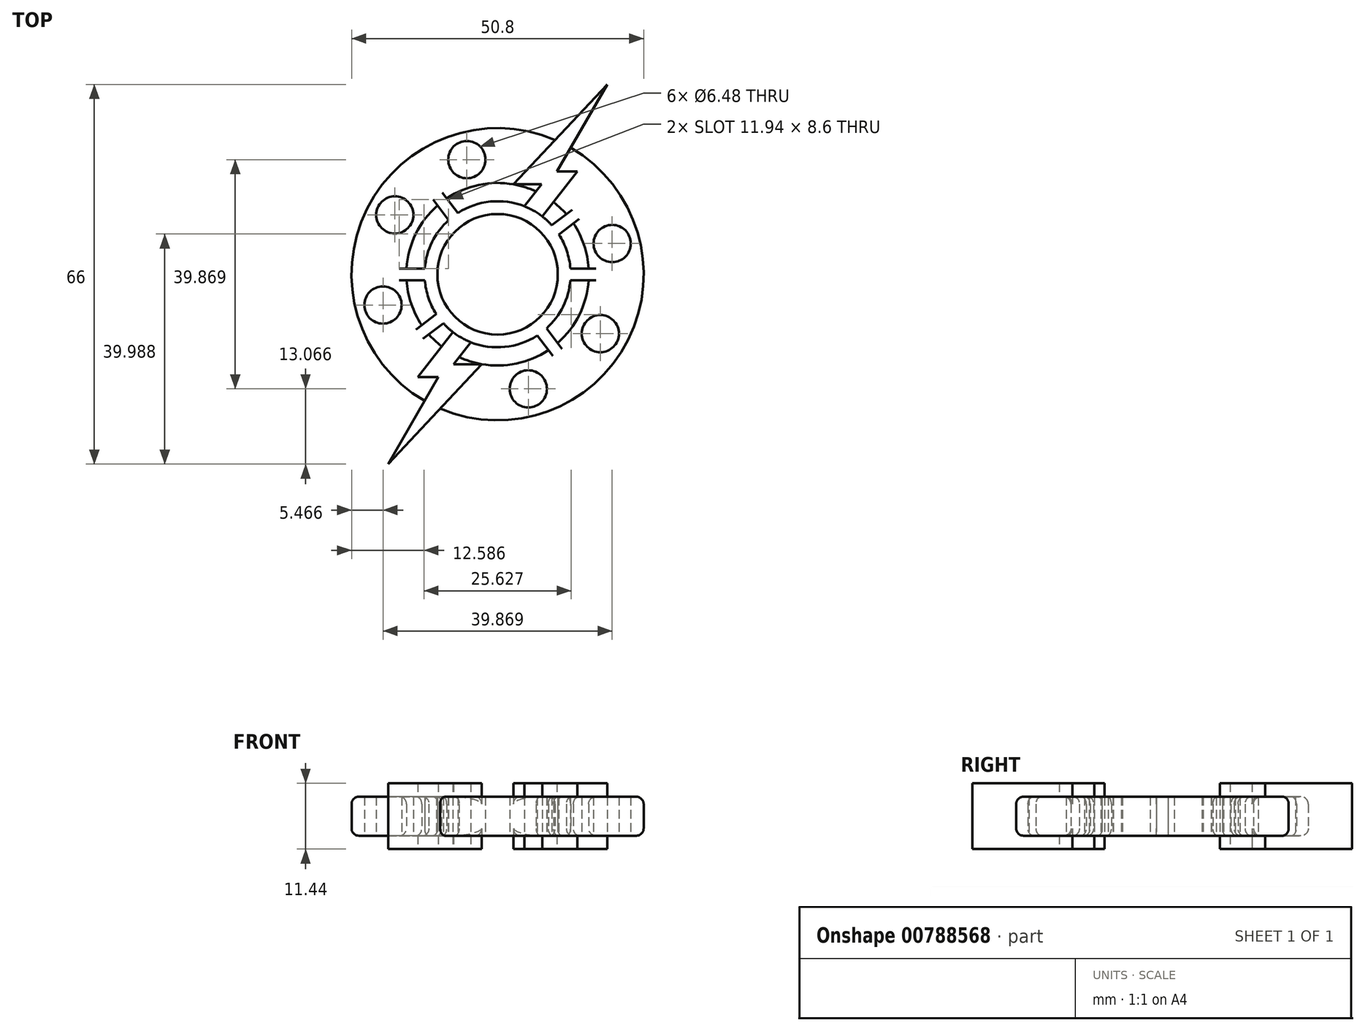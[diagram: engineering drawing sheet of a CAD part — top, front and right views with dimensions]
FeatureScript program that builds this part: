
annotation { "Feature Type Name" : "Feature", "Feature Type Description" : "" }
export const myFeature = defineFeature(function(context is Context, id is Id, definition is map)
    precondition{}
    {
        {
            var Q0;
            Q0=qCreatedBy(makeId("Top.planeOp"),FACE);
            var sketch = newSketch(context, id + "F0", { "sketchPlane" : qUnion([Q0])});
            skCircle(sketch, "E0", {"center": v(0, 0) * mm, "radius": 25.4 * mm});
            skCircle(sketch, "E1", {"center": v(0, 0) * mm, "radius": 15.88 * mm});
            skLineSegment(sketch, "E2", {"start": v(19.05, 33) * mm, "end": v(2.78, 15.63) * mm});
            skLineSegment(sketch, "E3", {"start": v(2.78, 15.63) * mm, "end": v(7.63, 15.63) * mm});
            skLineSegment(sketch, "E4", {"start": v(7.63, 15.63) * mm, "end": v(3.22, 9.97) * mm});
            skLineSegment(sketch, "E5", {"start": v(19.05, 33) * mm, "end": v(10.33, 17.89) * mm});
            skLineSegment(sketch, "E6", {"start": v(10.33, 17.89) * mm, "end": v(13.9, 17.89) * mm});
            skLineSegment(sketch, "E7", {"start": v(13.9, 17.89) * mm, "end": v(6.42, 8.28) * mm});
            skLineSegment(sketch, "E8.trimOffspring", {"start": v(10.33, 17.89) * mm, "end": v(19.05, 33) * mm});
            skLineSegment(sketch, "E9.1.0", {"start": v(-7.63, -15.63) * mm, "end": v(-3.22, -9.97) * mm});
            skLineSegment(sketch, "E9.1.1", {"start": v(-2.78, -15.63) * mm, "end": v(-7.63, -15.63) * mm});
            skLineSegment(sketch, "E9.1.2", {"start": v(-19.05, -33) * mm, "end": v(-2.78, -15.63) * mm});
            skLineSegment(sketch, "E9.1.3", {"start": v(-10.33, -17.89) * mm, "end": v(-19.05, -33) * mm});
            skLineSegment(sketch, "E9.1.4", {"start": v(-10.33, -17.89) * mm, "end": v(-13.9, -17.89) * mm});
            skLineSegment(sketch, "E9.1.5", {"start": v(-13.9, -17.89) * mm, "end": v(-6.42, -8.28) * mm});
            skCircle(sketch, "E10", {"center": v(0, 0) * mm, "radius": 10.48 * mm});
            skCircle(sketch, "E11", {"center": v(0, 0) * mm, "radius": 12.7 * mm});
            skLineSegment(sketch, "E12", {"start": v(0, 0) * mm, "end": v(19.05, 33) * mm, "construction": true});
            skLineSegment(sketch, "E13", {"start": v(0, 0) * mm, "end": v(-19.05, -33) * mm, "construction": true});
            skCircle(sketch, "E14", {"center": v(-17.87, 10.32) * mm, "radius": 3.24 * mm});
            skCircle(sketch, "E15", {"center": v(0, 0) * mm, "radius": 20.64 * mm, "construction": true});
            skCircle(sketch, "E16", {"center": v(-5.34, 19.93) * mm, "radius": 3.24 * mm});
            skCircle(sketch, "E17", {"center": v(-19.93, -5.34) * mm, "radius": 3.24 * mm});
            skCircle(sketch, "E18", {"center": v(5.34, -19.93) * mm, "radius": 3.24 * mm});
            skCircle(sketch, "E19", {"center": v(17.87, -10.32) * mm, "radius": 3.24 * mm});
            skCircle(sketch, "E20", {"center": v(19.93, 5.34) * mm, "radius": 3.24 * mm});
            skPoint(sketch, "E21.middle", {"position": v(-15.88, 0) * mm});
            skLineSegment(sketch, "E22.bottom", {"start": v(-10.43, 1.02) * mm, "end": v(-21.32, 1.02) * mm});
            skLineSegment(sketch, "E22.top", {"start": v(-10.43, -1.02) * mm, "end": v(-21.32, -1.02) * mm});
            skLineSegment(sketch, "E22.left", {"start": v(-10.43, 1.02) * mm, "end": v(-10.43, -1.02) * mm});
            skLineSegment(sketch, "E22.right", {"start": v(-21.32, 1.02) * mm, "end": v(-21.32, -1.02) * mm});
            skLineSegment(sketch, "E23.bottom", {"start": v(10.43, 1.02) * mm, "end": v(21.32, 1.02) * mm});
            skLineSegment(sketch, "E23.top", {"start": v(10.43, -1.02) * mm, "end": v(21.32, -1.02) * mm});
            skLineSegment(sketch, "E23.left", {"start": v(10.43, 1.02) * mm, "end": v(10.43, -1.02) * mm});
            skLineSegment(sketch, "E23.right", {"start": v(21.32, 1.02) * mm, "end": v(21.32, -1.02) * mm});
            skPoint(sketch, "E23.middle", {"position": v(15.88, 0) * mm});
            skLineSegment(sketch, "E24", {"start": v(-17.87, 10.32) * mm, "end": v(-5.34, 19.93) * mm, "construction": true});
            skLineSegment(sketch, "E25", {"start": v(0, 0) * mm, "end": v(-11.6, 15.13) * mm, "construction": true});
            skLineSegment(sketch, "E26", {"start": v(-11.6, 15.13) * mm, "end": v(-8.34, 10.88) * mm, "construction": true});
            skLineSegment(sketch, "E27", {"start": v(5.34, -19.93) * mm, "end": v(17.87, -10.32) * mm, "construction": true});
            skLineSegment(sketch, "E28", {"start": v(6.9, -10.66) * mm, "end": v(8.84, -13.19) * mm});
            skLineSegment(sketch, "E29", {"start": v(8.84, -13.19) * mm, "end": v(10.45, -11.95) * mm});
            skLineSegment(sketch, "E30", {"start": v(10.45, -11.95) * mm, "end": v(8.51, -9.42) * mm});
            skLineSegment(sketch, "E31", {"start": v(8.51, -9.42) * mm, "end": v(6.9, -10.66) * mm});
            skLineSegment(sketch, "E32", {"start": v(-8.51, 9.42) * mm, "end": v(-6.9, 10.66) * mm});
            skLineSegment(sketch, "E33", {"start": v(-5.49, 8.93) * mm, "end": v(-7.2, 7.61) * mm});
            skLineSegment(sketch, "E34", {"start": v(-8.51, 9.42) * mm, "end": v(-10.45, 11.95) * mm});
            skLineSegment(sketch, "E35", {"start": v(-10.45, 11.95) * mm, "end": v(-8.84, 13.19) * mm});
            skLineSegment(sketch, "E36", {"start": v(-8.84, 13.19) * mm, "end": v(-6.9, 10.66) * mm});
            skLineSegment(sketch, "E37", {"start": v(6.9, -10.66) * mm, "end": v(6.11, -9.63) * mm});
            skLineSegment(sketch, "E38", {"start": v(6.11, -9.63) * mm, "end": v(9.47, -14) * mm});
            skLineSegment(sketch, "E39", {"start": v(9.47, -14) * mm, "end": v(11.08, -12.77) * mm});
            skLineSegment(sketch, "E40", {"start": v(11.08, -12.77) * mm, "end": v(7.72, -8.4) * mm});
            skLineSegment(sketch, "E41", {"start": v(7.72, -8.4) * mm, "end": v(6.11, -9.63) * mm});
            skLineSegment(sketch, "E42", {"start": v(-8.51, 9.42) * mm, "end": v(-7.9, 8.64) * mm});
            skLineSegment(sketch, "E43", {"start": v(-7.9, 8.64) * mm, "end": v(-11.17, 12.89) * mm});
            skLineSegment(sketch, "E44", {"start": v(-8.84, 13.19) * mm, "end": v(-6.63, 10.31) * mm});
            skLineSegment(sketch, "E45", {"start": v(-6.63, 10.31) * mm, "end": v(-9.9, 14.56) * mm});
            skLineSegment(sketch, "E46", {"start": v(-11.17, 12.89) * mm, "end": v(-9.56, 14.12) * mm});
            skLineSegment(sketch, "E47", {"start": v(-9.56, 14.12) * mm, "end": v(-6.63, 10.31) * mm});
            skLineSegment(sketch, "E48", {"start": v(-6.63, 10.31) * mm, "end": v(-8.24, 9.08) * mm});
            skLineSegment(sketch, "E49", {"start": v(0, 0) * mm, "end": v(10.63, -13.85) * mm, "construction": true});
            skLineSegment(sketch, "E50", {"start": v(0, 0) * mm, "end": v(16.37, 12.56) * mm, "construction": true});
            skLineSegment(sketch, "E51", {"start": v(16.37, 12.56) * mm, "end": v(-12.6, -9.66) * mm, "construction": true});
            skLineSegment(sketch, "E52", {"start": v(14.21, 10.9) * mm, "end": v(13.6, 11.71) * mm});
            skLineSegment(sketch, "E53", {"start": v(13.6, 11.71) * mm, "end": v(8.35, 7.69) * mm});
            skLineSegment(sketch, "E54", {"start": v(8.35, 7.69) * mm, "end": v(9.6, 6.09) * mm});
            skLineSegment(sketch, "E55", {"start": v(14.21, 10.9) * mm, "end": v(14.83, 10.1) * mm});
            skLineSegment(sketch, "E56", {"start": v(14.83, 10.1) * mm, "end": v(9.6, 6.09) * mm});
            skLineSegment(sketch, "E57", {"start": v(-13.22, -11.42) * mm, "end": v(-8.13, -7.52) * mm});
            skLineSegment(sketch, "E58", {"start": v(-8.13, -7.52) * mm, "end": v(-9.37, -5.9) * mm});
            skLineSegment(sketch, "E59", {"start": v(-9.37, -5.9) * mm, "end": v(-14.45, -9.8) * mm});
            skLineSegment(sketch, "E60", {"start": v(-14.45, -9.8) * mm, "end": v(-13.22, -11.42) * mm});
            skSolve(sketch);
        }
        {
            var Q0;
            {var subQ0=sQuery(id+"F0.wireOp",EDGE,"E7");var subQ1=sQuery(id+"F0.wireOp",EDGE,"E1");var subQ2=makeQuery(id+"F0.imprint","INTERSECT",VERTEX,{"derivedFrom":[subQ1,subQ0]});Q0=makeQuery(id+"F0.imprint","IMPRINT",FACE,{"disambiguationData":[TD([[makeQuery(id+"F0.imprint","IMPRINT",EDGE,{"disambiguationData":[TD([[subQ2,-1.0]])],"derivedFrom":subQ1}),1.0]])]});}
            var Q1;
            {var subQ0=sQuery(id+"F0.wireOp",EDGE,"E22.bottom");var subQ1=sQuery(id+"F0.wireOp",EDGE,"E1");var subQ2=makeQuery(id+"F0.imprint","INTERSECT",VERTEX,{"derivedFrom":[subQ1,subQ0]});Q1=makeQuery(id+"F0.imprint","IMPRINT",FACE,{"disambiguationData":[TD([[makeQuery(id+"F0.imprint","IMPRINT",EDGE,{"disambiguationData":[TD([[subQ2,-1.0]])],"derivedFrom":subQ1}),1.0]])]});}
            var Q2;
            {var subQ0=sQuery(id+"F0.wireOp",EDGE,"E9.1.5");var subQ1=sQuery(id+"F0.wireOp",EDGE,"E1");var subQ2=makeQuery(id+"F0.imprint","INTERSECT",VERTEX,{"derivedFrom":[subQ1,subQ0]});Q2=makeQuery(id+"F0.imprint","IMPRINT",FACE,{"disambiguationData":[TD([[makeQuery(id+"F0.imprint","IMPRINT",EDGE,{"disambiguationData":[TD([[subQ2,-1.0]])],"derivedFrom":subQ1}),1.0]])]});}
            var Q3;
            {var subQ0=sQuery(id+"F0.wireOp",EDGE,"E23.bottom");var subQ1=sQuery(id+"F0.wireOp",EDGE,"E1");var subQ2=makeQuery(id+"F0.imprint","INTERSECT",VERTEX,{"derivedFrom":[subQ1,subQ0]});Q3=makeQuery(id+"F0.imprint","IMPRINT",FACE,{"disambiguationData":[TD([[makeQuery(id+"F0.imprint","IMPRINT",EDGE,{"disambiguationData":[TD([[subQ2,1.0]])],"derivedFrom":subQ1}),1.0]])]});}
            var Q4;
            {var subQ0=sQuery(id+"F0.wireOp",EDGE,"E2");var subQ1=sQuery(id+"F0.wireOp",EDGE,"E0");var subQ2=makeQuery(id+"F0.imprint","INTERSECT",VERTEX,{"derivedFrom":[subQ1,subQ0]});Q4=makeQuery(id+"F0.imprint","IMPRINT",FACE,{"disambiguationData":[TD([[makeQuery(id+"F0.imprint","IMPRINT",EDGE,{"disambiguationData":[TD([[subQ2,1.0]])],"derivedFrom":subQ1}),-1.0]])]});}
            var Q5;
            {var subQ0=sQuery(id+"F0.wireOp",EDGE,"E9.1.3");var subQ1=sQuery(id+"F0.wireOp",EDGE,"E0");var subQ2=makeQuery(id+"F0.imprint","INTERSECT",VERTEX,{"derivedFrom":[subQ1,subQ0]});Q5=makeQuery(id+"F0.imprint","IMPRINT",FACE,{"disambiguationData":[TD([[makeQuery(id+"F0.imprint","IMPRINT",EDGE,{"disambiguationData":[TD([[subQ2,-1.0]])],"derivedFrom":subQ1}),-1.0]])]});}
            var Q6;
            {var subQ0=sQuery(id+"F0.wireOp",EDGE,"E3");Q6=makeQuery(id+"F0.imprint","IMPRINT",FACE,{"disambiguationData":[TD([[makeQuery(id+"F0.imprint","IMPRINT",EDGE,{"derivedFrom":subQ0}),1.0]])]});}
            var Q7;
            {var subQ0=sQuery(id+"F0.wireOp",EDGE,"E9.1.1");Q7=makeQuery(id+"F0.imprint","IMPRINT",FACE,{"disambiguationData":[TD([[makeQuery(id+"F0.imprint","IMPRINT",EDGE,{"derivedFrom":subQ0}),1.0]])]});}
            var Q8;
            {var subQ0=sQuery(id+"F0.wireOp",EDGE,"E9.1.4");Q8=makeQuery(id+"F0.imprint","IMPRINT",FACE,{"disambiguationData":[TD([[makeQuery(id+"F0.imprint","IMPRINT",EDGE,{"derivedFrom":subQ0}),1.0]])]});}
            var Q9;
            {var subQ1=sQuery(id+"F0.wireOp",EDGE,"E6");Q9=makeQuery(id+"F0.imprint","IMPRINT",FACE,{"disambiguationData":[TD([[makeQuery(id+"F0.imprint","IMPRINT",EDGE,{"derivedFrom":subQ1}),1.0]])]});}
            var Q10;
            {var subQ0=sQuery(id+"F0.wireOp",EDGE,"E9.1.1");Q10=makeQuery(id+"F0.imprint","IMPRINT",FACE,{"disambiguationData":[TD([[makeQuery(id+"F0.imprint","IMPRINT",EDGE,{"derivedFrom":subQ0}),-1.0]])]});}
            var Q11;
            {var subQ0=sQuery(id+"F0.wireOp",EDGE,"E3");Q11=makeQuery(id+"F0.imprint","IMPRINT",FACE,{"disambiguationData":[TD([[makeQuery(id+"F0.imprint","IMPRINT",EDGE,{"derivedFrom":subQ0}),-1.0]])]});}
            var Q12;
            {var subQ5=sQuery(id+"F0.wireOp",EDGE,"E22.right");Q12=makeQuery(id+"F0.imprint","IMPRINT",FACE,{"disambiguationData":[TD([[makeQuery(id+"F0.imprint","IMPRINT",EDGE,{"derivedFrom":subQ5}),1.0]])]});}
            var Q13;
            {var subQ1=sQuery(id+"F0.wireOp",EDGE,"E22.bottom");var subQ6=sQuery(id+"F0.wireOp",EDGE,"E11");var subQ7=makeQuery(id+"F0.imprint","INTERSECT",VERTEX,{"derivedFrom":[subQ6,subQ1]});Q13=makeQuery(id+"F0.imprint","IMPRINT",FACE,{"disambiguationData":[TD([[makeQuery(id+"F0.imprint","IMPRINT",EDGE,{"disambiguationData":[TD([[subQ7,-1.0]])],"derivedFrom":subQ6}),1.0]])]});}
            var Q14;
            {var subQ0=sQuery(id+"F0.wireOp",EDGE,"E10");var subQ1=sQuery(id+"F0.wireOp",EDGE,"E9.1.5");var subQ2=makeQuery(id+"F0.imprint","INTERSECT",VERTEX,{"derivedFrom":[subQ1,subQ0]});Q14=makeQuery(id+"F0.imprint","IMPRINT",FACE,{"disambiguationData":[TD([[makeQuery(id+"F0.imprint","IMPRINT",EDGE,{"disambiguationData":[TD([[subQ2,1.0]])],"derivedFrom":subQ1}),1.0]])]});}
            var Q15;
            {var subQ0=sQuery(id+"F0.wireOp",EDGE,"E10");var subQ1=sQuery(id+"F0.wireOp",EDGE,"E4");var subQ2=makeQuery(id+"F0.imprint","INTERSECT",VERTEX,{"derivedFrom":[subQ1,subQ0]});Q15=makeQuery(id+"F0.imprint","IMPRINT",FACE,{"disambiguationData":[TD([[makeQuery(id+"F0.imprint","IMPRINT",EDGE,{"disambiguationData":[TD([[subQ2,1.0]])],"derivedFrom":subQ1}),-1.0]])]});}
            var Q16;
            {var subQ0=sQuery(id+"F0.wireOp",EDGE,"E10");var subQ1=sQuery(id+"F0.wireOp",EDGE,"E7");var subQ2=makeQuery(id+"F0.imprint","INTERSECT",VERTEX,{"derivedFrom":[subQ1,subQ0]});Q16=makeQuery(id+"F0.imprint","IMPRINT",FACE,{"disambiguationData":[TD([[makeQuery(id+"F0.imprint","IMPRINT",EDGE,{"disambiguationData":[TD([[subQ2,1.0]])],"derivedFrom":subQ1}),1.0]])]});}
            var Q17;
            {var subQ0=sQuery(id+"F0.wireOp",EDGE,"E10");var subQ1=sQuery(id+"F0.wireOp",EDGE,"E9.1.0");var subQ2=makeQuery(id+"F0.imprint","INTERSECT",VERTEX,{"derivedFrom":[subQ1,subQ0]});Q17=makeQuery(id+"F0.imprint","IMPRINT",FACE,{"disambiguationData":[TD([[makeQuery(id+"F0.imprint","IMPRINT",EDGE,{"disambiguationData":[TD([[subQ2,1.0]])],"derivedFrom":subQ1}),-1.0]])]});}
            var Q18;
            {var subQ1=sQuery(id+"F0.wireOp",EDGE,"E23.bottom");var subQ6=sQuery(id+"F0.wireOp",EDGE,"E11");var subQ7=makeQuery(id+"F0.imprint","INTERSECT",VERTEX,{"derivedFrom":[subQ6,subQ1]});Q18=makeQuery(id+"F0.imprint","IMPRINT",FACE,{"disambiguationData":[TD([[makeQuery(id+"F0.imprint","IMPRINT",EDGE,{"disambiguationData":[TD([[subQ7,1.0]])],"derivedFrom":subQ6}),1.0]])]});}
            var Q19;
            {var subQ0=sQuery(id+"F0.wireOp",EDGE,"E10");var subQ1=sQuery(id+"F0.wireOp",EDGE,"E9.1.0");var subQ2=makeQuery(id+"F0.imprint","INTERSECT",VERTEX,{"derivedFrom":[subQ1,subQ0]});Q19=makeQuery(id+"F0.imprint","IMPRINT",FACE,{"disambiguationData":[TD([[makeQuery(id+"F0.imprint","IMPRINT",EDGE,{"disambiguationData":[TD([[subQ2,1.0]])],"derivedFrom":subQ1}),1.0]])]});}
            var Q20;
            {var subQ0=sQuery(id+"F0.wireOp",EDGE,"E10");var subQ1=sQuery(id+"F0.wireOp",EDGE,"E4");var subQ2=makeQuery(id+"F0.imprint","INTERSECT",VERTEX,{"derivedFrom":[subQ1,subQ0]});Q20=makeQuery(id+"F0.imprint","IMPRINT",FACE,{"disambiguationData":[TD([[makeQuery(id+"F0.imprint","IMPRINT",EDGE,{"disambiguationData":[TD([[subQ2,1.0]])],"derivedFrom":subQ1}),1.0]])]});}
            var Q21;
            {var subQ5=sQuery(id+"F0.wireOp",EDGE,"E23.right");Q21=makeQuery(id+"F0.imprint","IMPRINT",FACE,{"disambiguationData":[TD([[makeQuery(id+"F0.imprint","IMPRINT",EDGE,{"derivedFrom":subQ5}),-1.0]])]});}
            var Q22;
            {var subQ0=sQuery(id+"F0.wireOp",EDGE,"E34");Q22=makeQuery(id+"F0.imprint","IMPRINT",FACE,{"disambiguationData":[TD([[makeQuery(id+"F0.imprint","IMPRINT",EDGE,{"derivedFrom":subQ0}),-1.0]])]});}
            var Q23;
            {var subQ1=sQuery(id+"F0.wireOp",EDGE,"E28");Q23=makeQuery(id+"F0.imprint","IMPRINT",FACE,{"disambiguationData":[TD([[makeQuery(id+"F0.imprint","IMPRINT",EDGE,{"derivedFrom":subQ1}),1.0]])]});}
            var Q24;
            {var subQ6=sQuery(id+"F0.wireOp",EDGE,"E35");Q24=makeQuery(id+"F0.imprint","IMPRINT",FACE,{"disambiguationData":[TD([[makeQuery(id+"F0.imprint","IMPRINT",EDGE,{"derivedFrom":subQ6}),-1.0]])]});}
            var Q25;
            {var subQ6=sQuery(id+"F0.wireOp",EDGE,"E29");Q25=makeQuery(id+"F0.imprint","IMPRINT",FACE,{"disambiguationData":[TD([[makeQuery(id+"F0.imprint","IMPRINT",EDGE,{"derivedFrom":subQ6}),1.0]])]});}
            var Q26;
            {var subQ0=sQuery(id+"F0.wireOp",EDGE,"E31");Q26=makeQuery(id+"F0.imprint","IMPRINT",FACE,{"disambiguationData":[TD([[makeQuery(id+"F0.imprint","IMPRINT",EDGE,{"derivedFrom":subQ0}),-1.0]])]});}
            var Q27;
            {var subQ6=sQuery(id+"F0.wireOp",EDGE,"E39");Q27=makeQuery(id+"F0.imprint","IMPRINT",FACE,{"disambiguationData":[TD([[makeQuery(id+"F0.imprint","IMPRINT",EDGE,{"derivedFrom":subQ6}),1.0]])]});}
            var Q28;
            {var subQ6=sQuery(id+"F0.wireOp",EDGE,"E46");Q28=makeQuery(id+"F0.imprint","IMPRINT",FACE,{"disambiguationData":[TD([[makeQuery(id+"F0.imprint","IMPRINT",EDGE,{"derivedFrom":subQ6}),-1.0]])]});}
            var Q29;
            {var subQ0=sQuery(id+"F0.wireOp",EDGE,"E32");Q29=makeQuery(id+"F0.imprint","IMPRINT",FACE,{"disambiguationData":[TD([[makeQuery(id+"F0.imprint","IMPRINT",EDGE,{"derivedFrom":subQ0}),-1.0]])]});}
            var Q30;
            {var subQ0=sQuery(id+"F0.wireOp",EDGE,"E35");Q30=makeQuery(id+"F0.imprint","IMPRINT",FACE,{"disambiguationData":[TD([[makeQuery(id+"F0.imprint","IMPRINT",EDGE,{"derivedFrom":subQ0}),1.0]])]});}
            var Q31;
            {var subQ0=sQuery(id+"F0.wireOp",EDGE,"E32");Q31=makeQuery(id+"F0.imprint","IMPRINT",FACE,{"disambiguationData":[TD([[makeQuery(id+"F0.imprint","IMPRINT",EDGE,{"derivedFrom":subQ0}),1.0]])]});}
            var Q32;
            {var subQ0=sQuery(id+"F0.wireOp",EDGE,"E29");Q32=makeQuery(id+"F0.imprint","IMPRINT",FACE,{"disambiguationData":[TD([[makeQuery(id+"F0.imprint","IMPRINT",EDGE,{"derivedFrom":subQ0}),-1.0]])]});}
            var Q33;
            {var subQ0=sQuery(id+"F0.wireOp",EDGE,"E31");Q33=makeQuery(id+"F0.imprint","IMPRINT",FACE,{"disambiguationData":[TD([[makeQuery(id+"F0.imprint","IMPRINT",EDGE,{"derivedFrom":subQ0}),1.0]])]});}
            var Q34;
            {var subQ5=sQuery(id+"F0.wireOp",EDGE,"E60");Q34=makeQuery(id+"F0.imprint","IMPRINT",FACE,{"disambiguationData":[TD([[makeQuery(id+"F0.imprint","IMPRINT",EDGE,{"derivedFrom":subQ5}),1.0]])]});}
            var Q35;
            {var subQ0=sQuery(id+"F0.wireOp",EDGE,"E59");var subQ1=sQuery(id+"F0.wireOp",EDGE,"E1");var subQ2=makeQuery(id+"F0.imprint","INTERSECT",VERTEX,{"derivedFrom":[subQ1,subQ0]});Q35=makeQuery(id+"F0.imprint","IMPRINT",FACE,{"disambiguationData":[TD([[makeQuery(id+"F0.imprint","IMPRINT",EDGE,{"disambiguationData":[TD([[subQ2,-1.0]])],"derivedFrom":subQ1}),1.0]])]});}
            var Q36;
            {var subQ5=sQuery(id+"F0.wireOp",EDGE,"E58");Q36=makeQuery(id+"F0.imprint","IMPRINT",FACE,{"disambiguationData":[TD([[makeQuery(id+"F0.imprint","IMPRINT",EDGE,{"derivedFrom":subQ5}),1.0]])]});}
            var Q37;
            {var subQ1=sQuery(id+"F0.wireOp",EDGE,"E52");Q37=makeQuery(id+"F0.imprint","IMPRINT",FACE,{"disambiguationData":[TD([[makeQuery(id+"F0.imprint","IMPRINT",EDGE,{"derivedFrom":subQ1}),1.0]])]});}
            var Q38;
            {var subQ0=sQuery(id+"F0.wireOp",EDGE,"E56");var subQ1=sQuery(id+"F0.wireOp",EDGE,"E1");var subQ2=makeQuery(id+"F0.imprint","INTERSECT",VERTEX,{"derivedFrom":[subQ1,subQ0]});Q38=makeQuery(id+"F0.imprint","IMPRINT",FACE,{"disambiguationData":[TD([[makeQuery(id+"F0.imprint","IMPRINT",EDGE,{"disambiguationData":[TD([[subQ2,-1.0]])],"derivedFrom":subQ1}),1.0]])]});}
            var Q39;
            {var subQ5=sQuery(id+"F0.wireOp",EDGE,"E54");Q39=makeQuery(id+"F0.imprint","IMPRINT",FACE,{"disambiguationData":[TD([[makeQuery(id+"F0.imprint","IMPRINT",EDGE,{"derivedFrom":subQ5}),1.0]])]});}
            extrude(context, id + "F1", {"entities" : qUnion([Q0, Q1, Q2, Q3, Q4, Q5, Q6, Q7, Q8, Q9, Q10, Q11, Q12, Q13, Q14, Q15, Q16, Q17, Q18, Q19, Q20, Q21, Q22, Q23, Q24, Q25, Q26, Q27, Q28, Q29, Q30, Q31, Q32, Q33, Q34, Q35, Q36, Q37, Q38, Q39]), "endBound" : BoundingType.SYMMETRIC, "depth" : 6.78 * mm, "offsetDistance" : 25.4 * mm});
        }
        {
            var Q0;
            {var subQ0=sQuery(id+"F0.wireOp",EDGE,"E0");Q0=makeQuery(id+"F1.opExtrude","CAP_EDGE",EDGE,{"disambiguationData":[OSD([subQ0]),TDD([makeQuery(id+"F0.imprint","IMPRINT",EDGE,{"disambiguationData":[TD([[makeQuery(id+"F0.imprint","INTERSECT",VERTEX,{"derivedFrom":[subQ0,sQuery(id+"F0.wireOp",EDGE,"9OY4pERo-kJL2-yspi-eJad-0AwwjGiXad2f")]}),1.0]])],"derivedFrom":subQ0}),makeQuery(id+"F0.imprint","IMPRINT",EDGE,{"disambiguationData":[TD([[makeQuery(id+"F0.imprint","INTERSECT",VERTEX,{"derivedFrom":[subQ0,sQuery(id+"F0.wireOp",EDGE,"QpBqrZuW-gGmc-8HGG-WRxZ-yx94tdyeTWWI")]}),-1.0]])],"derivedFrom":subQ0})])],"isStart":false});}
            var Q1;
            {var subQ0=sQuery(id+"F0.wireOp",EDGE,"E0");Q1=makeQuery(id+"F1.opExtrude","CAP_EDGE",EDGE,{"disambiguationData":[OSD([subQ0]),TDD([makeQuery(id+"F0.imprint","IMPRINT",EDGE,{"disambiguationData":[TD([[makeQuery(id+"F0.imprint","INTERSECT",VERTEX,{"derivedFrom":[subQ0,sQuery(id+"F0.wireOp",EDGE,"zZF1REFx-iCcK-emtb-jLQ4-MP0uSksG5p0N")]}),-1.0]])],"derivedFrom":subQ0})])],"isStart":false});}
            var Q2;
            {var subQ0=sQuery(id+"F0.wireOp",EDGE,"E1");Q2=makeQuery(id+"F1.opExtrude","CAP_EDGE",EDGE,{"disambiguationData":[OSD([subQ0]),TDD([makeQuery(id+"F0.imprint","IMPRINT",EDGE,{"disambiguationData":[TD([[makeQuery(id+"F0.imprint","INTERSECT",VERTEX,{"derivedFrom":[subQ0,sQuery(id+"F0.wireOp",EDGE,"E7")]}),1.0]])],"derivedFrom":subQ0})])],"isStart":false});}
            var Q3;
            {var subQ0=sQuery(id+"F0.wireOp",EDGE,"E1");Q3=makeQuery(id+"F1.opExtrude","CAP_EDGE",EDGE,{"disambiguationData":[OSD([subQ0]),TDD([makeQuery(id+"F0.imprint","IMPRINT",EDGE,{"disambiguationData":[TD([[makeQuery(id+"F0.imprint","INTERSECT",VERTEX,{"derivedFrom":[subQ0,sQuery(id+"F0.wireOp",EDGE,"E23.top")]}),1.0]])],"derivedFrom":subQ0})])],"isStart":false});}
            var Q4;
            {var subQ0=sQuery(id+"F0.wireOp",EDGE,"E1");var subQ1=makeQuery(id+"F0.imprint","INTERSECT",VERTEX,{"derivedFrom":[subQ0,sQuery(id+"F0.wireOp",EDGE,"E9.1.1"),sQuery(id+"F0.wireOp",EDGE,"E9.1.2")]});Q4=makeQuery(id+"F1.opExtrude","CAP_EDGE",EDGE,{"disambiguationData":[OSD([subQ0]),TDD([makeQuery(id+"F0.imprint","IMPRINT",EDGE,{"disambiguationData":[TD([[makeQuery(id+"F0.imprint","INTERSECT",VERTEX,{"derivedFrom":[subQ0,sQuery(id+"F0.wireOp",EDGE,"E9.1.0")]}),-1.0]])],"derivedFrom":subQ0}),makeQuery(id+"F0.imprint","IMPRINT",EDGE,{"disambiguationData":[TD([[subQ1,-1.0]])],"derivedFrom":subQ0})])],"isStart":false});}
            var Q5;
            {var subQ0=sQuery(id+"F0.wireOp",EDGE,"E1");Q5=makeQuery(id+"F1.opExtrude","CAP_EDGE",EDGE,{"disambiguationData":[OSD([subQ0]),TDD([makeQuery(id+"F0.imprint","IMPRINT",EDGE,{"disambiguationData":[TD([[makeQuery(id+"F0.imprint","INTERSECT",VERTEX,{"derivedFrom":[subQ0,sQuery(id+"F0.wireOp",EDGE,"E22.top")]}),-1.0]])],"derivedFrom":subQ0})])],"isStart":false});}
            var Q6;
            {var subQ0=sQuery(id+"F0.wireOp",EDGE,"E1");Q6=makeQuery(id+"F1.opExtrude","CAP_EDGE",EDGE,{"disambiguationData":[OSD([subQ0]),TDD([makeQuery(id+"F0.imprint","IMPRINT",EDGE,{"disambiguationData":[TD([[makeQuery(id+"F0.imprint","INTERSECT",VERTEX,{"derivedFrom":[subQ0,sQuery(id+"F0.wireOp",EDGE,"E22.bottom")]}),1.0]])],"derivedFrom":subQ0})])],"isStart":false});}
            var Q7;
            {var subQ0=sQuery(id+"F0.wireOp",EDGE,"E1");var subQ1=makeQuery(id+"F0.imprint","INTERSECT",VERTEX,{"derivedFrom":[subQ0,sQuery(id+"F0.wireOp",EDGE,"E2"),sQuery(id+"F0.wireOp",EDGE,"E3")]});Q7=makeQuery(id+"F1.opExtrude","CAP_EDGE",EDGE,{"disambiguationData":[OSD([subQ0]),TDD([makeQuery(id+"F0.imprint","IMPRINT",EDGE,{"disambiguationData":[TD([[makeQuery(id+"F0.imprint","INTERSECT",VERTEX,{"derivedFrom":[subQ0,sQuery(id+"F0.wireOp",EDGE,"E4")]}),-1.0]])],"derivedFrom":subQ0}),makeQuery(id+"F0.imprint","IMPRINT",EDGE,{"disambiguationData":[TD([[subQ1,-1.0]])],"derivedFrom":subQ0})])],"isStart":false});}
            var Q8;
            {var subQ0=sQuery(id+"F0.wireOp",EDGE,"E1");var subQ1=makeQuery(id+"F0.imprint","INTERSECT",VERTEX,{"derivedFrom":[subQ0,sQuery(id+"F0.wireOp",EDGE,"E2"),sQuery(id+"F0.wireOp",EDGE,"E3")]});Q8=makeQuery(id+"F1.opExtrude","CAP_EDGE",EDGE,{"disambiguationData":[OSD([subQ0]),TDD([makeQuery(id+"F0.imprint","IMPRINT",EDGE,{"disambiguationData":[TD([[makeQuery(id+"F0.imprint","INTERSECT",VERTEX,{"derivedFrom":[subQ0,sQuery(id+"F0.wireOp",EDGE,"E4")]}),-1.0]])],"derivedFrom":subQ0}),makeQuery(id+"F0.imprint","IMPRINT",EDGE,{"disambiguationData":[TD([[subQ1,-1.0]])],"derivedFrom":subQ0})])],"isStart":true});}
            var Q9;
            {var subQ0=sQuery(id+"F0.wireOp",EDGE,"E1");Q9=makeQuery(id+"F1.opExtrude","CAP_EDGE",EDGE,{"disambiguationData":[OSD([subQ0]),TDD([makeQuery(id+"F0.imprint","IMPRINT",EDGE,{"disambiguationData":[TD([[makeQuery(id+"F0.imprint","INTERSECT",VERTEX,{"derivedFrom":[subQ0,sQuery(id+"F0.wireOp",EDGE,"E22.bottom")]}),1.0]])],"derivedFrom":subQ0})])],"isStart":true});}
            var Q10;
            {var subQ0=sQuery(id+"F0.wireOp",EDGE,"E1");Q10=makeQuery(id+"F1.opExtrude","CAP_EDGE",EDGE,{"disambiguationData":[OSD([subQ0]),TDD([makeQuery(id+"F0.imprint","IMPRINT",EDGE,{"disambiguationData":[TD([[makeQuery(id+"F0.imprint","INTERSECT",VERTEX,{"derivedFrom":[subQ0,sQuery(id+"F0.wireOp",EDGE,"E22.top")]}),-1.0]])],"derivedFrom":subQ0})])],"isStart":true});}
            var Q11;
            {var subQ0=sQuery(id+"F0.wireOp",EDGE,"E1");Q11=makeQuery(id+"F1.opExtrude","CAP_EDGE",EDGE,{"disambiguationData":[OSD([subQ0]),TDD([makeQuery(id+"F0.imprint","IMPRINT",EDGE,{"disambiguationData":[TD([[makeQuery(id+"F0.imprint","INTERSECT",VERTEX,{"derivedFrom":[subQ0,sQuery(id+"F0.wireOp",EDGE,"E7")]}),1.0]])],"derivedFrom":subQ0})])],"isStart":true});}
            var Q12;
            {var subQ0=sQuery(id+"F0.wireOp",EDGE,"E1");Q12=makeQuery(id+"F1.opExtrude","CAP_EDGE",EDGE,{"disambiguationData":[OSD([subQ0]),TDD([makeQuery(id+"F0.imprint","IMPRINT",EDGE,{"disambiguationData":[TD([[makeQuery(id+"F0.imprint","INTERSECT",VERTEX,{"derivedFrom":[subQ0,sQuery(id+"F0.wireOp",EDGE,"E23.top")]}),1.0]])],"derivedFrom":subQ0})])],"isStart":true});}
            var Q13;
            {var subQ0=sQuery(id+"F0.wireOp",EDGE,"E1");var subQ1=makeQuery(id+"F0.imprint","INTERSECT",VERTEX,{"derivedFrom":[subQ0,sQuery(id+"F0.wireOp",EDGE,"E9.1.1"),sQuery(id+"F0.wireOp",EDGE,"E9.1.2")]});Q13=makeQuery(id+"F1.opExtrude","CAP_EDGE",EDGE,{"disambiguationData":[OSD([subQ0]),TDD([makeQuery(id+"F0.imprint","IMPRINT",EDGE,{"disambiguationData":[TD([[makeQuery(id+"F0.imprint","INTERSECT",VERTEX,{"derivedFrom":[subQ0,sQuery(id+"F0.wireOp",EDGE,"E9.1.0")]}),-1.0]])],"derivedFrom":subQ0}),makeQuery(id+"F0.imprint","IMPRINT",EDGE,{"disambiguationData":[TD([[subQ1,-1.0]])],"derivedFrom":subQ0})])],"isStart":true});}
            fillet(context, id + "F2", {"entities" : qUnion([Q0, Q1, Q2, Q3, Q4, Q5, Q6, Q7, Q8, Q9, Q10, Q11, Q12, Q13]), "radius" : 1.27 * mm, "tangentPropagation" : true, "allowEdgeOverflow" : false});
        }
        {
            var Q0;
            {var subQ0=sQuery(id+"F0.wireOp",EDGE,"E3");Q0=makeQuery(id+"F0.imprint","IMPRINT",FACE,{"disambiguationData":[TD([[makeQuery(id+"F0.imprint","IMPRINT",EDGE,{"derivedFrom":subQ0}),1.0]])]});}
            var Q1;
            {var subQ0=sQuery(id+"F0.wireOp",EDGE,"E2");var subQ1=sQuery(id+"F0.wireOp",EDGE,"E0");var subQ2=makeQuery(id+"F0.imprint","INTERSECT",VERTEX,{"derivedFrom":[subQ1,subQ0]});Q1=makeQuery(id+"F0.imprint","IMPRINT",FACE,{"disambiguationData":[TD([[makeQuery(id+"F0.imprint","IMPRINT",EDGE,{"disambiguationData":[TD([[subQ2,1.0]])],"derivedFrom":subQ1}),-1.0]])]});}
            var Q2;
            {var subQ0=sQuery(id+"F0.wireOp",EDGE,"E9.1.1");Q2=makeQuery(id+"F0.imprint","IMPRINT",FACE,{"disambiguationData":[TD([[makeQuery(id+"F0.imprint","IMPRINT",EDGE,{"derivedFrom":subQ0}),1.0]])]});}
            var Q3;
            {var subQ0=sQuery(id+"F0.wireOp",EDGE,"E9.1.3");var subQ1=sQuery(id+"F0.wireOp",EDGE,"E0");var subQ2=makeQuery(id+"F0.imprint","INTERSECT",VERTEX,{"derivedFrom":[subQ1,subQ0]});Q3=makeQuery(id+"F0.imprint","IMPRINT",FACE,{"disambiguationData":[TD([[makeQuery(id+"F0.imprint","IMPRINT",EDGE,{"disambiguationData":[TD([[subQ2,-1.0]])],"derivedFrom":subQ1}),-1.0]])]});}
            var Q4;
            {var subQ0=sQuery(id+"F0.wireOp",EDGE,"E4");var subQ1=sQuery(id+"F0.wireOp",EDGE,"E1");var subQ2=makeQuery(id+"F0.imprint","INTERSECT",VERTEX,{"derivedFrom":[subQ1,subQ0]});Q4=makeQuery(id+"F0.imprint","IMPRINT",FACE,{"disambiguationData":[TD([[makeQuery(id+"F0.imprint","IMPRINT",EDGE,{"disambiguationData":[TD([[subQ2,1.0]])],"derivedFrom":subQ1}),1.0]])]});}
            var Q5;
            {var subQ0=sQuery(id+"F0.wireOp",EDGE,"E9.1.5");var subQ1=sQuery(id+"F0.wireOp",EDGE,"E1");var subQ2=makeQuery(id+"F0.imprint","INTERSECT",VERTEX,{"derivedFrom":[subQ1,subQ0]});Q5=makeQuery(id+"F0.imprint","IMPRINT",FACE,{"disambiguationData":[TD([[makeQuery(id+"F0.imprint","IMPRINT",EDGE,{"disambiguationData":[TD([[subQ2,-1.0]])],"derivedFrom":subQ1}),1.0]])]});}
            extrude(context, id + "F3", {"entities" : qUnion([Q0, Q1, Q2, Q3, Q4, Q5]), "operationType" : NewBodyOperationType.ADD, "endBound" : BoundingType.SYMMETRIC, "depth" : 11.43 * mm, "offsetDistance" : 25.4 * mm});
        }
        {
            var Q0;
            {var subQ0=sQuery(id+"F0.wireOp",EDGE,"E10");var subQ1=sQuery(id+"F0.wireOp",EDGE,"E4");var subQ2=makeQuery(id+"F0.imprint","INTERSECT",VERTEX,{"derivedFrom":[subQ1,subQ0]});Q0=makeQuery(id+"F0.imprint","IMPRINT",FACE,{"disambiguationData":[TD([[makeQuery(id+"F0.imprint","IMPRINT",EDGE,{"disambiguationData":[TD([[subQ2,1.0]])],"derivedFrom":subQ1}),-1.0]])]});}
            var Q1;
            {var subQ0=sQuery(id+"F0.wireOp",EDGE,"E10");var subQ1=sQuery(id+"F0.wireOp",EDGE,"E9.1.0");var subQ2=makeQuery(id+"F0.imprint","INTERSECT",VERTEX,{"derivedFrom":[subQ1,subQ0]});Q1=makeQuery(id+"F0.imprint","IMPRINT",FACE,{"disambiguationData":[TD([[makeQuery(id+"F0.imprint","IMPRINT",EDGE,{"disambiguationData":[TD([[subQ2,1.0]])],"derivedFrom":subQ1}),1.0]])]});}
            var Q2;
            {var subQ0=sQuery(id+"F0.wireOp",EDGE,"E10");var subQ1=sQuery(id+"F0.wireOp",EDGE,"E7");var subQ2=makeQuery(id+"F0.imprint","INTERSECT",VERTEX,{"derivedFrom":[subQ1,subQ0]});Q2=makeQuery(id+"F0.imprint","IMPRINT",FACE,{"disambiguationData":[TD([[makeQuery(id+"F0.imprint","IMPRINT",EDGE,{"disambiguationData":[TD([[subQ2,1.0]])],"derivedFrom":subQ1}),1.0]])]});}
            var Q3;
            {var subQ0=sQuery(id+"F0.wireOp",EDGE,"E10");var subQ1=sQuery(id+"F0.wireOp",EDGE,"E4");var subQ2=makeQuery(id+"F0.imprint","INTERSECT",VERTEX,{"derivedFrom":[subQ1,subQ0]});Q3=makeQuery(id+"F0.imprint","IMPRINT",FACE,{"disambiguationData":[TD([[makeQuery(id+"F0.imprint","IMPRINT",EDGE,{"disambiguationData":[TD([[subQ2,1.0]])],"derivedFrom":subQ1}),1.0]])]});}
            var Q4;
            {var subQ1=sQuery(id+"F0.wireOp",EDGE,"E21.bottom");var subQ6=sQuery(id+"F0.wireOp",EDGE,"E11");var subQ7=makeQuery(id+"F0.imprint","INTERSECT",VERTEX,{"derivedFrom":[subQ6,subQ1]});Q4=makeQuery(id+"F0.imprint","IMPRINT",FACE,{"disambiguationData":[TD([[makeQuery(id+"F0.imprint","IMPRINT",EDGE,{"disambiguationData":[TD([[subQ7,-1.0]])],"derivedFrom":subQ6}),1.0]])]});}
            var Q5;
            {var subQ0=sQuery(id+"F0.wireOp",EDGE,"E10");var subQ1=sQuery(id+"F0.wireOp",EDGE,"E9.1.5");var subQ2=makeQuery(id+"F0.imprint","INTERSECT",VERTEX,{"derivedFrom":[subQ1,subQ0]});Q5=makeQuery(id+"F0.imprint","IMPRINT",FACE,{"disambiguationData":[TD([[makeQuery(id+"F0.imprint","IMPRINT",EDGE,{"disambiguationData":[TD([[subQ2,1.0]])],"derivedFrom":subQ1}),1.0]])]});}
            extrude(context, id + "F4", {"entities" : qUnion([Q0, Q1, Q2, Q3, Q4, Q5]), "operationType" : NewBodyOperationType.ADD, "endBound" : BoundingType.SYMMETRIC, "depth" : 6.78 * mm, "offsetDistance" : 25.4 * mm});
        }
        {
            var Q0;
            {var subQ1=sQuery(id+"F0.wireOp",EDGE,"E1");Q0=makeQuery(id+"F3.boolean.opBoolean","SPLIT",EDGE,{"disambiguationData":[TD([makeQuery(id+"F3.opExtrude","SWEPT_FACE",FACE,{"disambiguationData":[OSD([sQuery(id+"F0.wireOp",EDGE,"E9.1.5")])]})])],"derivedFrom":makeQuery(id+"F1.opExtrude","CAP_EDGE",EDGE,{"disambiguationData":[OSD([subQ1])],"isStart":false})});}
            var Q1;
            {var subQ0=sQuery(id+"F0.wireOp",EDGE,"E1");Q1=makeQuery(id+"F3.boolean.opBoolean","SPLIT",EDGE,{"disambiguationData":[TD([makeQuery(id+"F3.opExtrude","SWEPT_FACE",FACE,{"disambiguationData":[OSD([sQuery(id+"F0.wireOp",EDGE,"E7")])]})])],"derivedFrom":makeQuery(id+"F1.opExtrude","CAP_EDGE",EDGE,{"disambiguationData":[OSD([subQ0])],"isStart":false})});}
            var Q2;
            {var subQ1=sQuery(id+"F0.wireOp",EDGE,"E1");Q2=makeQuery(id+"F3.boolean.opBoolean","SPLIT",EDGE,{"disambiguationData":[TD([makeQuery(id+"F3.opExtrude","SWEPT_FACE",FACE,{"disambiguationData":[OSD([sQuery(id+"F0.wireOp",EDGE,"E9.1.5")])]})])],"derivedFrom":makeQuery(id+"F1.opExtrude","CAP_EDGE",EDGE,{"disambiguationData":[OSD([subQ1])],"isStart":true})});}
            var Q3;
            {var subQ1=sQuery(id+"F0.wireOp",EDGE,"E1");Q3=makeQuery(id+"F3.boolean.opBoolean","SPLIT",EDGE,{"disambiguationData":[TD([makeQuery(id+"F3.opExtrude","SWEPT_FACE",FACE,{"disambiguationData":[OSD([sQuery(id+"F0.wireOp",EDGE,"E7")])]})])],"derivedFrom":makeQuery(id+"F1.opExtrude","CAP_EDGE",EDGE,{"disambiguationData":[OSD([subQ1])],"isStart":true})});}
            var Q4;
            {var subQ0=sQuery(id+"F0.wireOp",EDGE,"E0");Q4=makeQuery(id+"F1.opExtrude","CAP_EDGE",EDGE,{"disambiguationData":[OSD([subQ0]),TDD([makeQuery(id+"F0.imprint","IMPRINT",EDGE,{"disambiguationData":[TD([[makeQuery(id+"F0.imprint","INTERSECT",VERTEX,{"derivedFrom":[subQ0,sQuery(id+"F0.wireOp",EDGE,"E8.trimOffspring")]}),1.0]])],"derivedFrom":subQ0})])],"isStart":true});}
            var Q5;
            {var subQ0=sQuery(id+"F0.wireOp",EDGE,"E0");Q5=makeQuery(id+"F1.opExtrude","CAP_EDGE",EDGE,{"disambiguationData":[OSD([subQ0]),TDD([makeQuery(id+"F0.imprint","IMPRINT",EDGE,{"disambiguationData":[TD([[makeQuery(id+"F0.imprint","INTERSECT",VERTEX,{"derivedFrom":[subQ0,sQuery(id+"F0.wireOp",EDGE,"E2")]}),-1.0]])],"derivedFrom":subQ0})])],"isStart":true});}
            fillet(context, id + "F5", {"entities" : qUnion([Q0, Q1, Q2, Q3, Q4, Q5]), "radius" : 1.27 * mm, "tangentPropagation" : true, "allowEdgeOverflow" : false});
        }
    });
